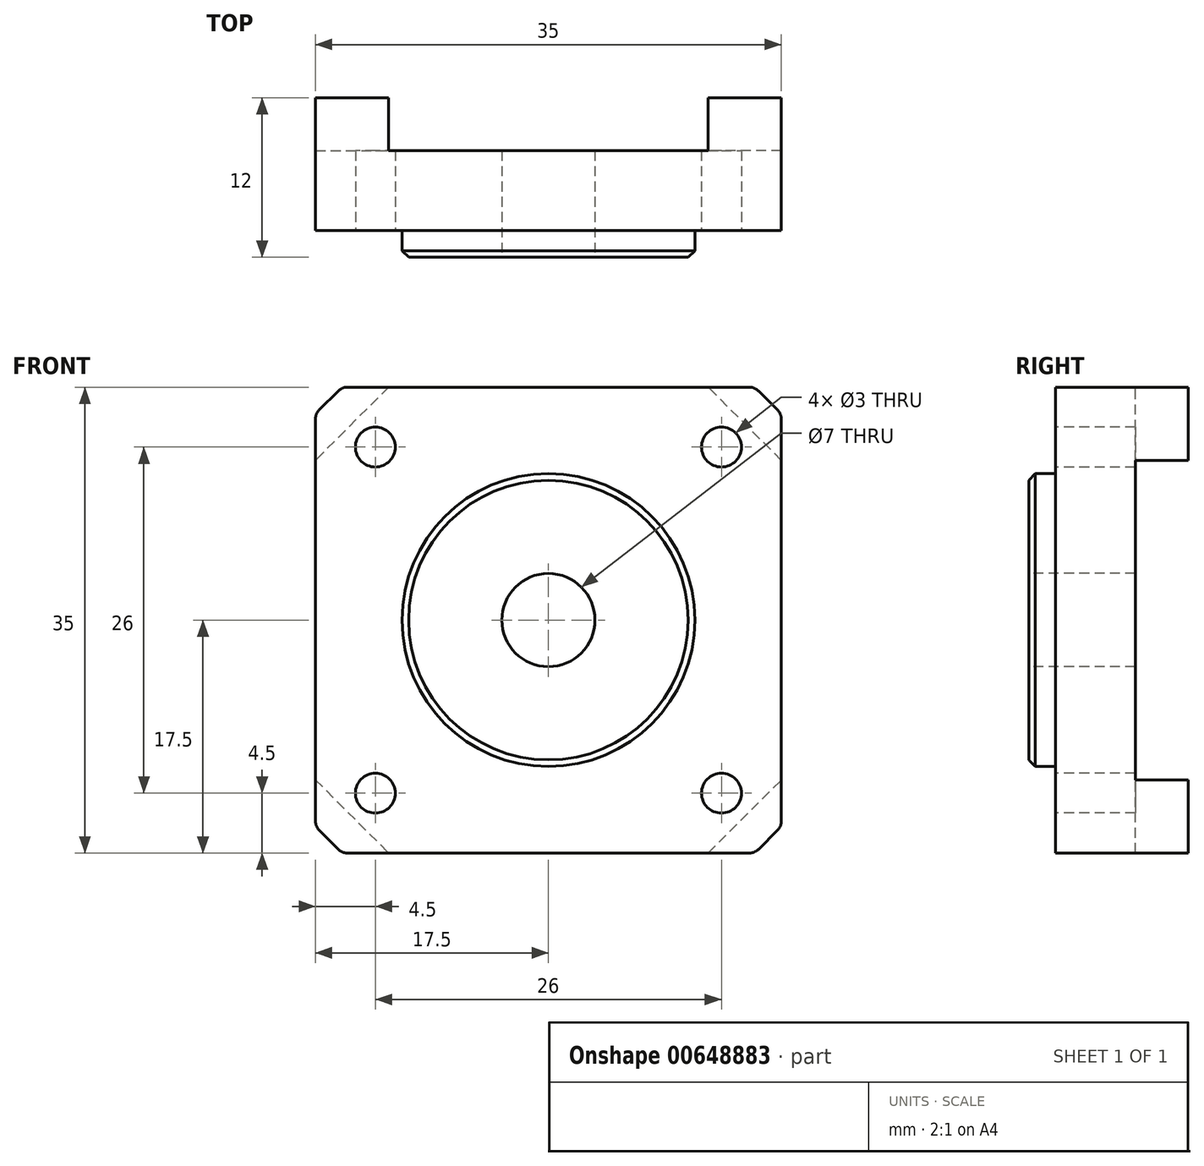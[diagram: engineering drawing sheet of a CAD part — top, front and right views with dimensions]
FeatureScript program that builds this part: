
annotation { "Feature Type Name" : "Feature", "Feature Type Description" : "" }
export const myFeature = defineFeature(function(context is Context, id is Id, definition is map)
    precondition{}
    {
        {
            var Q0;
            Q0=qCreatedBy(makeId("Front.planeOp"),FACE);
            var sketch = newSketch(context, id + "F0", { "sketchPlane" : qUnion([Q0])});
            skLineSegment(sketch, "E0.bottom", {"start": v(-17.5, 17.5) * mm, "end": v(17.5, 17.5) * mm});
            skLineSegment(sketch, "E0.top", {"start": v(-17.5, -17.5) * mm, "end": v(17.5, -17.5) * mm});
            skLineSegment(sketch, "E0.left", {"start": v(-17.5, 17.5) * mm, "end": v(-17.5, -17.5) * mm});
            skLineSegment(sketch, "E0.right", {"start": v(17.5, 17.5) * mm, "end": v(17.5, -17.5) * mm});
            skPoint(sketch, "E0.middle", {"position": v(0, 0) * mm});
            skSolve(sketch);
        }
        {
            var Q0;
            Q0=makeQuery(id+"F0.imprint","IMPRINT",FACE,{"disambiguationData":[TD([[makeQuery(id+"F0.imprint","IMPRINT",EDGE,{"derivedFrom":sQuery(id+"F0.wireOp",EDGE,"E0.bottom")}),-1.0]])]});
            extrude(context, id + "F1", {"entities" : qUnion([Q0]), "depth" : 10 * mm, "offsetDistance" : 25 * mm});
        }
        {
            var Q0;
            Q0=makeQuery(id+"F1.opExtrude","SWEPT_EDGE",EDGE,{"disambiguationData":[OSD([sQuery(id+"F0.wireOp",EDGE,"E0.bottom"),sQuery(id+"F0.wireOp",EDGE,"E0.left")])]});
            var Q1;
            Q1=makeQuery(id+"F1.opExtrude","SWEPT_EDGE",EDGE,{"disambiguationData":[OSD([sQuery(id+"F0.wireOp",EDGE,"E0.bottom"),sQuery(id+"F0.wireOp",EDGE,"E0.right")])]});
            var Q2;
            Q2=makeQuery(id+"F1.opExtrude","SWEPT_EDGE",EDGE,{"disambiguationData":[OSD([sQuery(id+"F0.wireOp",EDGE,"E0.top"),sQuery(id+"F0.wireOp",EDGE,"E0.right")])]});
            var Q3;
            Q3=makeQuery(id+"F1.opExtrude","SWEPT_EDGE",EDGE,{"disambiguationData":[OSD([sQuery(id+"F0.wireOp",EDGE,"E0.top"),sQuery(id+"F0.wireOp",EDGE,"E0.left")])]});
            chamfer(context, id + "F2", {"entities" : qUnion([Q0, Q1, Q2, Q3]), "width" : 2 * mm, "tangentPropagation" : true});
        }
        {
            var Q0;
            Q0=makeQuery(id+"F1.opExtrude","CAP_FACE",FACE,{"disambiguationData":[OSD([sQuery(id+"F0.wireOp",EDGE,"E0.bottom"),sQuery(id+"F0.wireOp",EDGE,"E0.top"),sQuery(id+"F0.wireOp",EDGE,"E0.left"),sQuery(id+"F0.wireOp",EDGE,"E0.right")])],"isStart":false});
            var sketch = newSketch(context, id + "F3", { "sketchPlane" : qUnion([Q0])});
            skCircle(sketch, "E1", {"center": v(0, 0) * mm, "radius": 11 * mm});
            skSolve(sketch);
        }
        {
            var Q0;
            Q0=makeQuery(id+"F3.imprint","IMPRINT",FACE,{"disambiguationData":[TD([[makeQuery(id+"F3.imprint","IMPRINT",EDGE,{"derivedFrom":sQuery(id+"F3.wireOp",EDGE,"E1")}),1.0]])]});
            extrude(context, id + "F4", {"entities" : qUnion([Q0]), "operationType" : NewBodyOperationType.REMOVE, "oppositeDirection" : true, "depth" : 0.5 * mm, "offsetDistance" : 25 * mm});
        }
        {
            var Q0;
            Q0=makeQuery(id+"F4.boolean.opBoolean","COPY",FACE,{"derivedFrom":makeQuery(id+"F4.opExtrude","CAP_FACE",FACE,{"disambiguationData":[OSD([sQuery(id+"F3.wireOp",EDGE,"E1")])],"isStart":false})});
            var sketch = newSketch(context, id + "F5", { "sketchPlane" : qUnion([Q0])});
            skCircle(sketch, "E2", {"center": v(0, 0) * mm, "radius": 11 * mm});
            skSolve(sketch);
        }
        {
            var Q0;
            Q0=makeQuery(id+"F5.imprint","IMPRINT",FACE,{"disambiguationData":[TD([[makeQuery(id+"F5.imprint","IMPRINT",EDGE,{"derivedFrom":sQuery(id+"F5.wireOp",EDGE,"E2")}),1.0]])]});
            extrude(context, id + "F6", {"entities" : qUnion([Q0]), "operationType" : NewBodyOperationType.ADD, "depth" : 2.5 * mm, "offsetDistance" : 25 * mm});
        }
        {
            var Q0;
            Q0=makeQuery(id+"F6.opExtrude","CAP_FACE",FACE,{"disambiguationData":[OSD([sQuery(id+"F5.wireOp",EDGE,"E2")])],"isStart":false});
            var sketch = newSketch(context, id + "F7", { "sketchPlane" : qUnion([Q0])});
            skCircle(sketch, "E3", {"center": v(0, 0) * mm, "radius": 3.5 * mm});
            skSolve(sketch);
        }
        {
            var Q0;
            Q0=makeQuery(id+"F7.imprint","IMPRINT",FACE,{"disambiguationData":[TD([[makeQuery(id+"F7.imprint","IMPRINT",EDGE,{"derivedFrom":sQuery(id+"F7.wireOp",EDGE,"E3")}),1.0]])]});
            var Q1;
            Q1=sQuery(id+"F7.wireOp",EDGE,"E3");
            extrude(context, id + "F8", {"entities" : qUnion([Q0]), "operationType" : NewBodyOperationType.REMOVE, "surfaceEntities" : qUnion([Q1]), "endBound" : BoundingType.THROUGH_ALL, "oppositeDirection" : true, "depth" : 25 * mm, "offsetDistance" : 25 * mm});
        }
        {
            var Q0;
            {var subQ0=sQuery(id+"F0.wireOp",EDGE,"E0.bottom");Q0=makeQuery(id+"F2.opChamfer","BLEND_EDGE",EDGE,{"blendedFrom":[makeQuery(id+"F1.opExtrude","SWEPT_EDGE",EDGE,{"disambiguationData":[OSD([subQ0,sQuery(id+"F0.wireOp",EDGE,"E0.left")])]}),makeQuery(id+"F1.opExtrude","SWEPT_FACE",FACE,{"disambiguationData":[OSD([subQ0])]})],"blendedInto":[makeQuery(id+"F1.opExtrude","SWEPT_FACE",FACE,{"disambiguationData":[OSD([subQ0])]})]});}
            var Q1;
            {var subQ0=sQuery(id+"F0.wireOp",EDGE,"E0.bottom");Q1=makeQuery(id+"F2.opChamfer","BLEND_EDGE",EDGE,{"blendedFrom":[makeQuery(id+"F1.opExtrude","SWEPT_EDGE",EDGE,{"disambiguationData":[OSD([subQ0,sQuery(id+"F0.wireOp",EDGE,"E0.right")])]}),makeQuery(id+"F1.opExtrude","SWEPT_FACE",FACE,{"disambiguationData":[OSD([subQ0])]})],"blendedInto":[makeQuery(id+"F1.opExtrude","SWEPT_FACE",FACE,{"disambiguationData":[OSD([subQ0])]})]});}
            var Q2;
            {var subQ0=sQuery(id+"F0.wireOp",EDGE,"E0.right");Q2=makeQuery(id+"F2.opChamfer","BLEND_EDGE",EDGE,{"blendedFrom":[makeQuery(id+"F1.opExtrude","SWEPT_EDGE",EDGE,{"disambiguationData":[OSD([sQuery(id+"F0.wireOp",EDGE,"E0.bottom"),subQ0])]}),makeQuery(id+"F1.opExtrude","SWEPT_FACE",FACE,{"disambiguationData":[OSD([subQ0])]})],"blendedInto":[makeQuery(id+"F1.opExtrude","SWEPT_FACE",FACE,{"disambiguationData":[OSD([subQ0])]})]});}
            var Q3;
            {var subQ0=sQuery(id+"F0.wireOp",EDGE,"E0.right");Q3=makeQuery(id+"F2.opChamfer","BLEND_EDGE",EDGE,{"blendedFrom":[makeQuery(id+"F1.opExtrude","SWEPT_EDGE",EDGE,{"disambiguationData":[OSD([sQuery(id+"F0.wireOp",EDGE,"E0.top"),subQ0])]}),makeQuery(id+"F1.opExtrude","SWEPT_FACE",FACE,{"disambiguationData":[OSD([subQ0])]})],"blendedInto":[makeQuery(id+"F1.opExtrude","SWEPT_FACE",FACE,{"disambiguationData":[OSD([subQ0])]})]});}
            var Q4;
            {var subQ0=sQuery(id+"F0.wireOp",EDGE,"E0.top");Q4=makeQuery(id+"F2.opChamfer","BLEND_EDGE",EDGE,{"blendedFrom":[makeQuery(id+"F1.opExtrude","SWEPT_EDGE",EDGE,{"disambiguationData":[OSD([subQ0,sQuery(id+"F0.wireOp",EDGE,"E0.right")])]}),makeQuery(id+"F1.opExtrude","SWEPT_FACE",FACE,{"disambiguationData":[OSD([subQ0])]})],"blendedInto":[makeQuery(id+"F1.opExtrude","SWEPT_FACE",FACE,{"disambiguationData":[OSD([subQ0])]})]});}
            var Q5;
            {var subQ0=sQuery(id+"F0.wireOp",EDGE,"E0.top");Q5=makeQuery(id+"F2.opChamfer","BLEND_EDGE",EDGE,{"blendedFrom":[makeQuery(id+"F1.opExtrude","SWEPT_EDGE",EDGE,{"disambiguationData":[OSD([subQ0,sQuery(id+"F0.wireOp",EDGE,"E0.left")])]}),makeQuery(id+"F1.opExtrude","SWEPT_FACE",FACE,{"disambiguationData":[OSD([subQ0])]})],"blendedInto":[makeQuery(id+"F1.opExtrude","SWEPT_FACE",FACE,{"disambiguationData":[OSD([subQ0])]})]});}
            var Q6;
            {var subQ0=sQuery(id+"F0.wireOp",EDGE,"E0.left");Q6=makeQuery(id+"F2.opChamfer","BLEND_EDGE",EDGE,{"blendedFrom":[makeQuery(id+"F1.opExtrude","SWEPT_EDGE",EDGE,{"disambiguationData":[OSD([sQuery(id+"F0.wireOp",EDGE,"E0.top"),subQ0])]}),makeQuery(id+"F1.opExtrude","SWEPT_FACE",FACE,{"disambiguationData":[OSD([subQ0])]})],"blendedInto":[makeQuery(id+"F1.opExtrude","SWEPT_FACE",FACE,{"disambiguationData":[OSD([subQ0])]})]});}
            var Q7;
            {var subQ0=sQuery(id+"F0.wireOp",EDGE,"E0.left");Q7=makeQuery(id+"F2.opChamfer","BLEND_EDGE",EDGE,{"blendedFrom":[makeQuery(id+"F1.opExtrude","SWEPT_EDGE",EDGE,{"disambiguationData":[OSD([sQuery(id+"F0.wireOp",EDGE,"E0.bottom"),subQ0])]}),makeQuery(id+"F1.opExtrude","SWEPT_FACE",FACE,{"disambiguationData":[OSD([subQ0])]})],"blendedInto":[makeQuery(id+"F1.opExtrude","SWEPT_FACE",FACE,{"disambiguationData":[OSD([subQ0])]})]});}
            fillet(context, id + "F9", {"entities" : qUnion([Q0, Q1, Q2, Q3, Q4, Q5, Q6, Q7]), "radius" : 1 * mm, "tangentPropagation" : true, "allowEdgeOverflow" : false});
        }
        {
            var Q0;
            Q0=makeQuery(id+"F6.opExtrude","CAP_EDGE",EDGE,{"disambiguationData":[OSD([sQuery(id+"F5.wireOp",EDGE,"E2")])],"isStart":false});
            var Q1;
            Q1=makeQuery(id+"F8.boolean.opBoolean","COPY",EDGE,{"derivedFrom":makeQuery(id+"F8.opExtrude","CAP_EDGE",EDGE,{"disambiguationData":[OSD([sQuery(id+"F7.wireOp",EDGE,"E3")])],"isStart":true})});
            var Q2;
            Q2=makeQuery(id+"F6.opExtrude","CAP_EDGE",EDGE,{"disambiguationData":[OSD([sQuery(id+"F5.wireOp",EDGE,"E2")])],"isStart":true});
            chamfer(context, id + "F10", {"entities" : qUnion([Q0, Q1, Q2]), "width" : 0.5 * mm, "tangentPropagation" : true});
        }
        {
            var Q0;
            Q0=makeQuery(id+"F1.opExtrude","CAP_FACE",FACE,{"disambiguationData":[OSD([sQuery(id+"F0.wireOp",EDGE,"E0.bottom"),sQuery(id+"F0.wireOp",EDGE,"E0.top"),sQuery(id+"F0.wireOp",EDGE,"E0.left"),sQuery(id+"F0.wireOp",EDGE,"E0.right")])],"isStart":false});
            var sketch = newSketch(context, id + "F11", { "sketchPlane" : qUnion([Q0])});
            skCircle(sketch, "E4", {"center": v(-13, 13) * mm, "radius": 1.5 * mm});
            skCircle(sketch, "E5.1.0", {"center": v(-13, -13) * mm, "radius": 1.5 * mm});
            skCircle(sketch, "E5.2.0", {"center": v(13, -13) * mm, "radius": 1.5 * mm});
            skCircle(sketch, "E5.3.0", {"center": v(13, 13) * mm, "radius": 1.5 * mm});
            skPoint(sketch, "E5.center", {"position": v(0, 0) * mm});
            skSolve(sketch);
        }
        {
            var Q0;
            Q0=qSketchRegion(id+"F11",true);
            extrude(context, id + "F12", {"entities" : qUnion([Q0]), "operationType" : NewBodyOperationType.REMOVE, "endBound" : BoundingType.THROUGH_ALL, "oppositeDirection" : true, "depth" : 25 * mm, "offsetDistance" : 25 * mm});
        }
        {
            var Q0;
            Q0=makeQuery(id+"F1.opExtrude","CAP_FACE",FACE,{"disambiguationData":[OSD([sQuery(id+"F0.wireOp",EDGE,"E0.bottom"),sQuery(id+"F0.wireOp",EDGE,"E0.top"),sQuery(id+"F0.wireOp",EDGE,"E0.left"),sQuery(id+"F0.wireOp",EDGE,"E0.right")])],"isStart":true});
            var sketch = newSketch(context, id + "F13", { "sketchPlane" : qUnion([Q0])});
            skLineSegment(sketch, "E6.bottom", {"start": v(-12, 17.5) * mm, "end": v(12, 17.5) * mm});
            skLineSegment(sketch, "E6.top", {"start": v(-12, -17.5) * mm, "end": v(12, -17.5) * mm});
            skLineSegment(sketch, "E6.left", {"start": v(-17.5, 12) * mm, "end": v(-17.5, -12) * mm});
            skLineSegment(sketch, "E6.right", {"start": v(17.5, 12) * mm, "end": v(17.5, -12) * mm});
            skPoint(sketch, "E6.middle", {"position": v(0, 0) * mm});
            skLineSegment(sketch, "E7", {"start": v(-17.5, 12) * mm, "end": v(-12, 17.5) * mm});
            skLineSegment(sketch, "E8.1.0", {"start": v(-12, -17.5) * mm, "end": v(-17.5, -12) * mm});
            skLineSegment(sketch, "E8.2.0", {"start": v(17.5, -12) * mm, "end": v(12, -17.5) * mm});
            skLineSegment(sketch, "E8.3.0", {"start": v(12, 17.5) * mm, "end": v(17.5, 12) * mm});
            skPoint(sketch, "E9.orphan", {"position": v(-17.5, 17.5) * mm});
            skPoint(sketch, "E10.orphan", {"position": v(-17.5, -17.5) * mm});
            skPoint(sketch, "E11.orphan", {"position": v(17.5, -17.5) * mm});
            skPoint(sketch, "E12.orphan", {"position": v(17.5, 17.5) * mm});
            skSolve(sketch);
        }
        {
            var Q0;
            Q0 = qSketchRegion(id + "F13", true);
            extrude(context, id + "F14", {"entities" : qUnion([Q0]), "operationType" : NewBodyOperationType.REMOVE, "oppositeDirection" : true, "depth" : 4 * mm, "offsetDistance" : 25 * mm});
        }
    });
